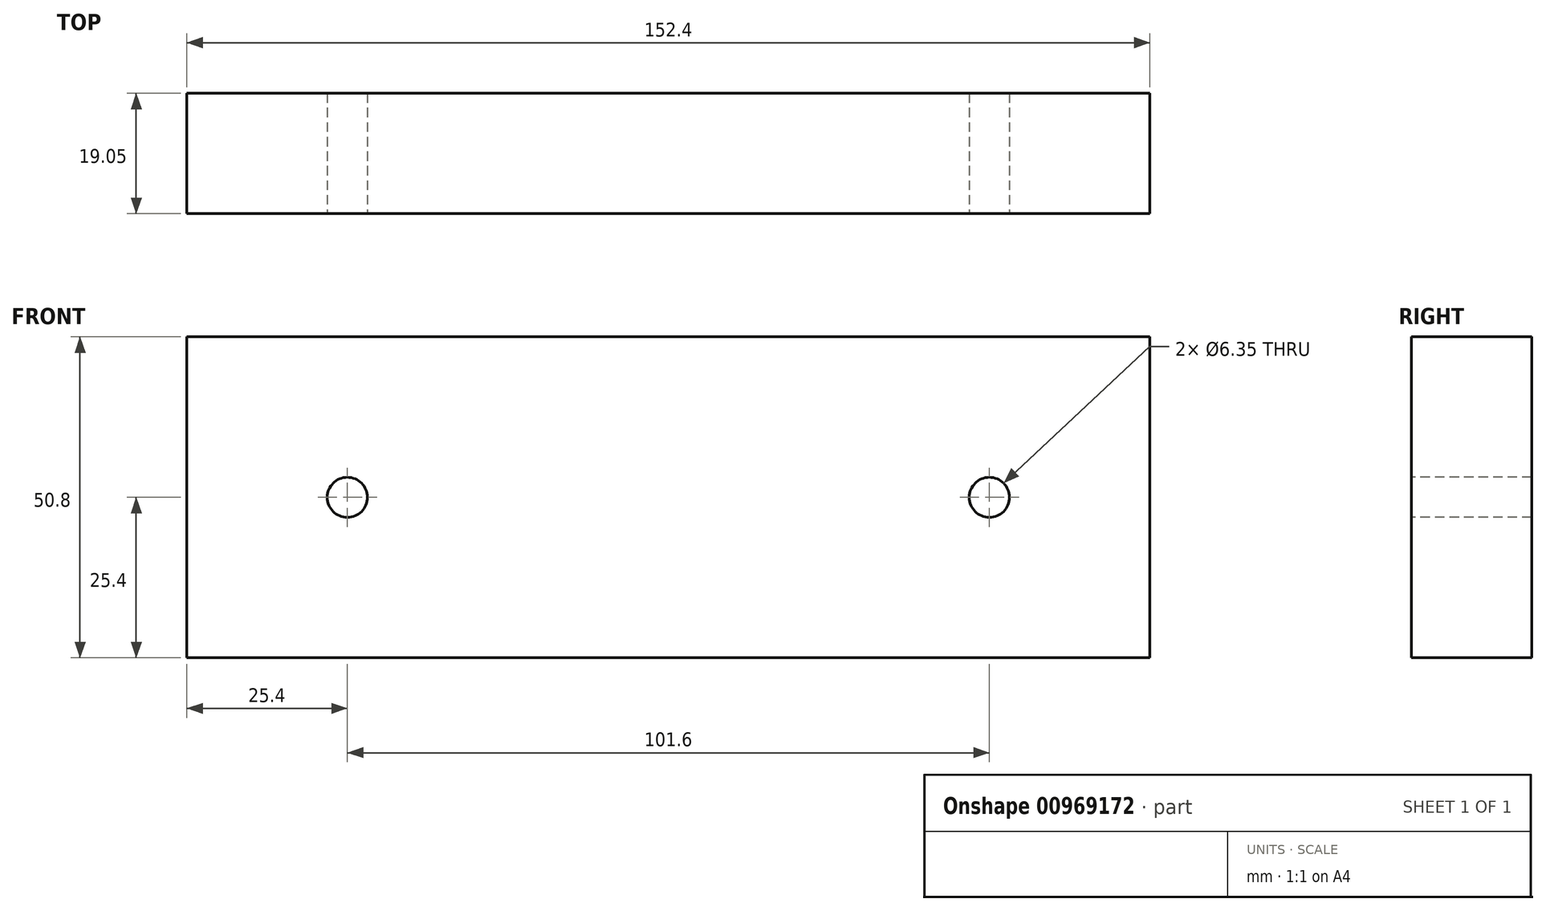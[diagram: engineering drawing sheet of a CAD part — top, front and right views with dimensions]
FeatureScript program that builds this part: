
annotation { "Feature Type Name" : "Feature", "Feature Type Description" : "" }
export const myFeature = defineFeature(function(context is Context, id is Id, definition is map)
    precondition{}
    {
        {
            var Q0;
            Q0=qCreatedBy(makeId("Front.planeOp"),FACE);
            var sketch = newSketch(context, id + "F0", { "sketchPlane" : qUnion([Q0])});
            skLineSegment(sketch, "E0.bottom", {"start": v(76.2, -25.4) * mm, "end": v(-76.2, -25.4) * mm});
            skLineSegment(sketch, "E0.top", {"start": v(76.2, 25.4) * mm, "end": v(-76.2, 25.4) * mm});
            skLineSegment(sketch, "E0.left", {"start": v(76.2, -25.4) * mm, "end": v(76.2, 25.4) * mm});
            skLineSegment(sketch, "E0.right", {"start": v(-76.2, -25.4) * mm, "end": v(-76.2, 25.4) * mm});
            skPoint(sketch, "E0.middle", {"position": v(0, 0) * mm});
            skSolve(sketch);
        }
        {
            var Q0;
            Q0 = qSketchRegion(id + "F0", true);
            extrude(context, id + "F1", {"entities" : qUnion([Q0]), "depth" : 19.05 * mm, "offsetDistance" : 25.4 * mm});
        }
        {
            var Q0;
            Q0=makeQuery(id+"F1.opExtrude","CAP_FACE",FACE,{"disambiguationData":[OSD([sQuery(id+"F0.wireOp",EDGE,"E0.bottom"),sQuery(id+"F0.wireOp",EDGE,"E0.top"),sQuery(id+"F0.wireOp",EDGE,"E0.left"),sQuery(id+"F0.wireOp",EDGE,"E0.right")])],"isStart":false});
            var sketch = newSketch(context, id + "F2", { "sketchPlane" : qUnion([Q0])});
            skPoint(sketch, "E1", {"position": v(-50.8, 0) * mm});
            skPoint(sketch, "E2", {"position": v(50.8, 0) * mm});
            skSolve(sketch);
        }
        {
            var Q0;
            Q0=sQuery(id+"F2.wireOp",VERTEX,"E1");
            var Q1;
            Q1=sQuery(id+"F2.wireOp",VERTEX,"E2");
            var Q2;
            Q2=makeQuery(id+"F1.opExtrude","SWEPT_BODY",BODY,{"disambiguationData":[OSD([sQuery(id+"F0.wireOp",EDGE,"E0.bottom"),sQuery(id+"F0.wireOp",EDGE,"E0.top"),sQuery(id+"F0.wireOp",EDGE,"E0.left"),sQuery(id+"F0.wireOp",EDGE,"E0.right")])]});
            hole(context, id + "F3", {"style" : HoleStyle.SIMPLE, "endStyle" : HoleEndStyle.THROUGH, "holeDiameter" : 6.35 * mm, "majorDiameter" : 6.35 * mm, "isTappedThrough" : true, "tappedDepth" : 12.7 * mm, "tapClearance" : 3, "locations" : qUnion([Q0, Q1]), "scope" : qUnion([Q2])});
        }
    });
